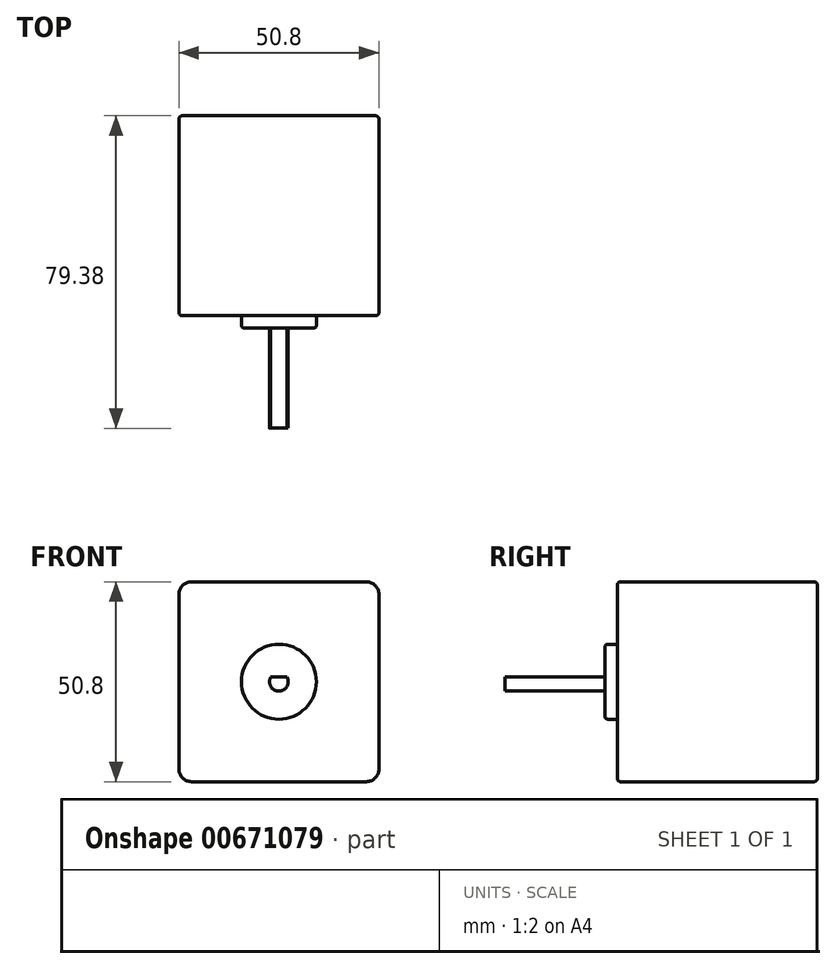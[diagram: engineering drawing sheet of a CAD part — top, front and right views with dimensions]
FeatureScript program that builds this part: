
annotation { "Feature Type Name" : "Feature", "Feature Type Description" : "" }
export const myFeature = defineFeature(function(context is Context, id is Id, definition is map)
    precondition{}
    {
        {
            var Q0;
            Q0=qCreatedBy(makeId("Front.planeOp"),FACE);
            var sketch = newSketch(context, id + "F0", { "sketchPlane" : qUnion([Q0])});
            skLineSegment(sketch, "E0.bottom", {"start": v(25.4, 25.4) * mm, "end": v(-25.4, 25.4) * mm});
            skLineSegment(sketch, "E0.top", {"start": v(25.4, -25.4) * mm, "end": v(-25.4, -25.4) * mm});
            skLineSegment(sketch, "E0.left", {"start": v(25.4, 25.4) * mm, "end": v(25.4, -25.4) * mm});
            skLineSegment(sketch, "E0.right", {"start": v(-25.4, 25.4) * mm, "end": v(-25.4, -25.4) * mm});
            skPoint(sketch, "E0.middle", {"position": v(0, 0) * mm});
            skCircle(sketch, "E1", {"center": v(0, 0) * mm, "radius": 9.53 * mm});
            skSolve(sketch);
        }
        {
            var Q0;
            Q0 = qSketchRegion(id + "F0", true);
            var Q1;
            Q1=makeQuery(id+"F0.imprint","IMPRINT",FACE,{"disambiguationData":[TD([[makeQuery(id+"F0.imprint","IMPRINT",EDGE,{"derivedFrom":sQuery(id+"F0.wireOp",EDGE,"E1")}),1.0]])]});
            extrude(context, id + "F1", {"entities" : qUnion([Q0, Q1]), "oppositeDirection" : true, "depth" : 50.8 * mm, "offsetDistance" : 25.4 * mm});
        }
        {
            var Q0;
            Q0=makeQuery(id+"F0.imprint","IMPRINT",FACE,{"disambiguationData":[TD([[makeQuery(id+"F0.imprint","IMPRINT",EDGE,{"derivedFrom":sQuery(id+"F0.wireOp",EDGE,"E1")}),1.0]])]});
            extrude(context, id + "F2", {"entities" : qUnion([Q0]), "operationType" : NewBodyOperationType.ADD, "depth" : 3.17 * mm, "offsetDistance" : 25.4 * mm});
        }
        {
            var Q0;
            Q0=makeQuery(id+"F2.opExtrude","CAP_FACE",FACE,{"disambiguationData":[OSD([sQuery(id+"F0.wireOp",EDGE,"E1")])],"isStart":false});
            var sketch = newSketch(context, id + "F3", { "sketchPlane" : qUnion([Q0])});
            skCircle(sketch, "E2", {"center": v(0, 0) * mm, "radius": 2.38 * mm});
            skSolve(sketch);
        }
        {
            var Q0;
            Q0 = qSketchRegion(id + "F3", true);
            extrude(context, id + "F4", {"entities" : qUnion([Q0]), "operationType" : NewBodyOperationType.ADD, "depth" : 25.4 * mm, "offsetDistance" : 25.4 * mm});
        }
        {
            var Q0;
            Q0=makeQuery(id+"F4.opExtrude","CAP_FACE",FACE,{"disambiguationData":[OSD([sQuery(id+"F3.wireOp",EDGE,"E2")])],"isStart":false});
            var sketch = newSketch(context, id + "F5", { "sketchPlane" : qUnion([Q0])});
            skLineSegment(sketch, "E3.bottom", {"start": v(-2.06, 1.2) * mm, "end": v(2.06, 1.2) * mm});
            skLineSegment(sketch, "E3.top", {"start": v(-2.06, 2.38) * mm, "end": v(2.06, 2.38) * mm});
            skLineSegment(sketch, "E3.left", {"start": v(-2.06, 1.2) * mm, "end": v(-2.06, 2.38) * mm});
            skLineSegment(sketch, "E3.right", {"start": v(2.06, 1.2) * mm, "end": v(2.06, 2.38) * mm});
            skSolve(sketch);
        }
        {
            var Q0;
            Q0 = qSketchRegion(id + "F5", true);
            var Q1;
            Q1=makeQuery(id+"F2.opExtrude","CAP_FACE",FACE,{"disambiguationData":[OSD([sQuery(id+"F0.wireOp",EDGE,"E1")])],"isStart":false});
            extrude(context, id + "F6", {"entities" : qUnion([Q0]), "operationType" : NewBodyOperationType.REMOVE, "endBound" : BoundingType.UP_TO_SURFACE, "oppositeDirection" : true, "depth" : 25.4 * mm, "endBoundEntityFace" : qUnion([Q1]), "offsetDistance" : 25.4 * mm});
        }
        {
            var Q0;
            Q0=makeQuery(id+"F1.opExtrude","SWEPT_EDGE",EDGE,{"disambiguationData":[OSD([sQuery(id+"F0.wireOp",EDGE,"E0.bottom"),sQuery(id+"F0.wireOp",EDGE,"E0.left")])]});
            var Q1;
            Q1=makeQuery(id+"F1.opExtrude","SWEPT_EDGE",EDGE,{"disambiguationData":[OSD([sQuery(id+"F0.wireOp",EDGE,"E0.top"),sQuery(id+"F0.wireOp",EDGE,"E0.left")])]});
            var Q2;
            Q2=makeQuery(id+"F1.opExtrude","SWEPT_EDGE",EDGE,{"disambiguationData":[OSD([sQuery(id+"F0.wireOp",EDGE,"E0.bottom"),sQuery(id+"F0.wireOp",EDGE,"E0.right")])]});
            var Q3;
            Q3=makeQuery(id+"F1.opExtrude","SWEPT_EDGE",EDGE,{"disambiguationData":[OSD([sQuery(id+"F0.wireOp",EDGE,"E0.top"),sQuery(id+"F0.wireOp",EDGE,"E0.right")])]});
            fillet(context, id + "F7", {"entities" : qUnion([Q0, Q1, Q2, Q3]), "radius" : 3.17 * mm, "tangentPropagation" : true, "allowEdgeOverflow" : false});
        }
        {
            var Q0;
            Q0=makeQuery(id+"F1.opExtrude","CAP_EDGE",EDGE,{"disambiguationData":[OSD([sQuery(id+"F0.wireOp",EDGE,"E0.bottom")])],"isStart":true});
            var Q1;
            Q1=makeQuery(id+"F1.opExtrude","CAP_EDGE",EDGE,{"disambiguationData":[OSD([sQuery(id+"F0.wireOp",EDGE,"E0.bottom")])],"isStart":false});
            var Q2;
            Q2=makeQuery(id+"F2.opExtrude","CAP_EDGE",EDGE,{"disambiguationData":[OSD([sQuery(id+"F0.wireOp",EDGE,"E1")])],"isStart":false});
            fillet(context, id + "F8", {"entities" : qUnion([Q0, Q1, Q2]), "radius" : 0.8 * mm, "tangentPropagation" : true, "allowEdgeOverflow" : false});
        }
    });
